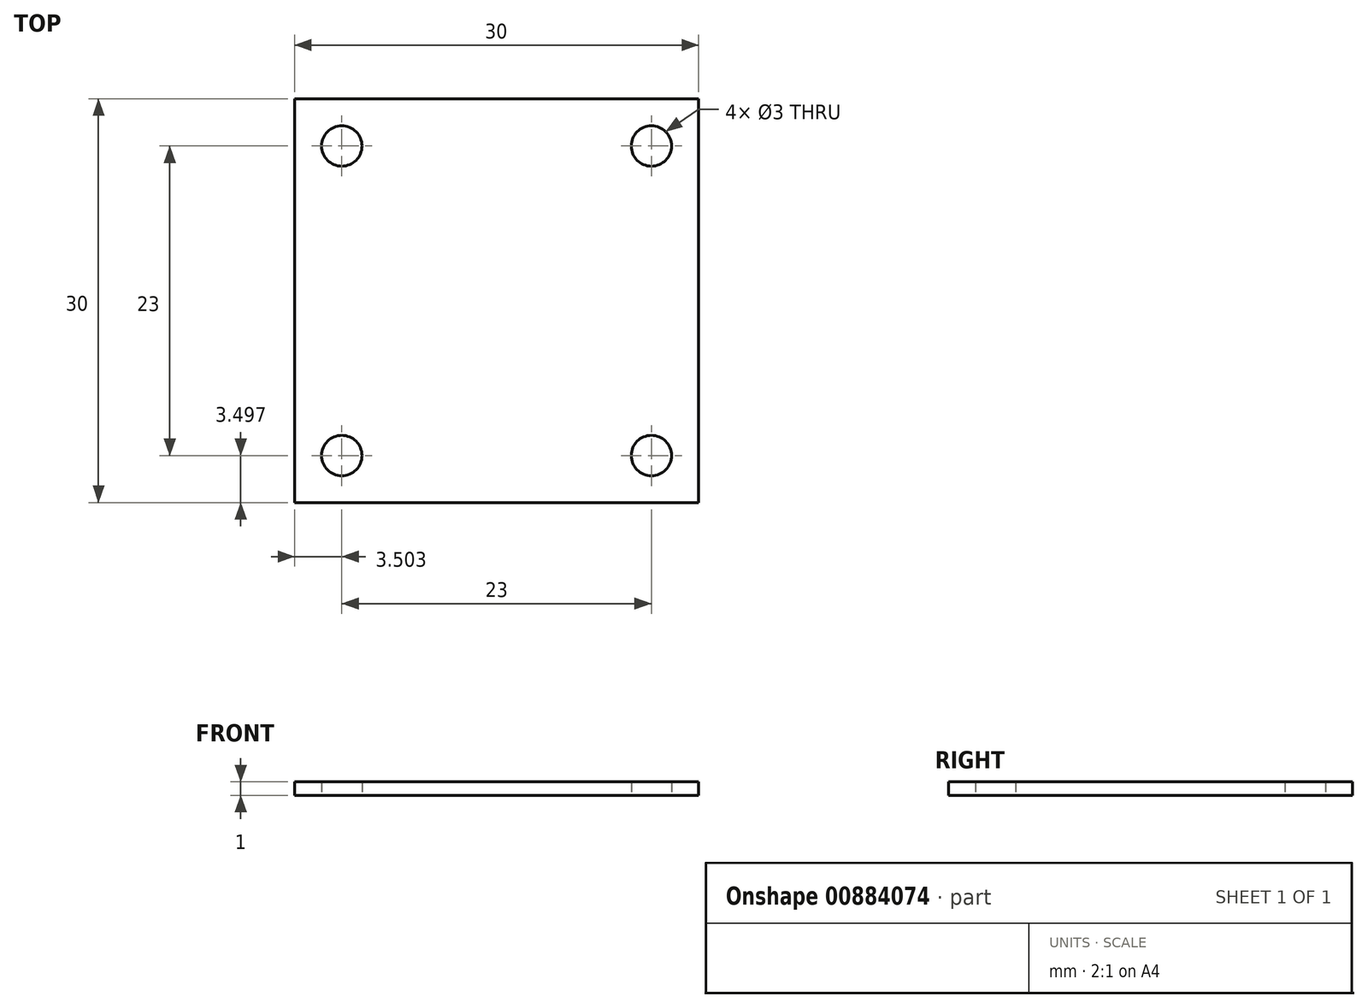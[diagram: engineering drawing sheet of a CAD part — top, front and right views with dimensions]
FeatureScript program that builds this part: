
annotation { "Feature Type Name" : "Feature", "Feature Type Description" : "" }
export const myFeature = defineFeature(function(context is Context, id is Id, definition is map)
    precondition{}
    {
        {
            var Q0;
            Q0=qCreatedBy(makeId("Top.planeOp"),FACE);
            var sketch = newSketch(context, id + "F0", { "sketchPlane" : qUnion([Q0])});
            skLineSegment(sketch, "E0.bottom", {"start": v(-40.86, 10.92) * mm, "end": v(-10.86, 10.92) * mm});
            skLineSegment(sketch, "E0.top", {"start": v(-40.86, -19.08) * mm, "end": v(-10.86, -19.08) * mm});
            skLineSegment(sketch, "E0.left", {"start": v(-40.86, 10.92) * mm, "end": v(-40.86, -19.08) * mm});
            skLineSegment(sketch, "E0.right", {"start": v(-10.86, 10.92) * mm, "end": v(-10.86, -19.08) * mm});
            skCircle(sketch, "E1", {"center": v(-14.36, 7.42) * mm, "radius": 1.5 * mm});
            skCircle(sketch, "E2.MirrorC", {"center": v(-37.36, 7.42) * mm, "radius": 1.5 * mm});
            skCircle(sketch, "E3.MirrorC", {"center": v(-14.36, -15.58) * mm, "radius": 1.5 * mm});
            skCircle(sketch, "E4.MirrorC", {"center": v(-37.36, -15.58) * mm, "radius": 1.5 * mm});
            skSolve(sketch);
        }
        {
            var Q0;
            Q0 = qSketchRegion(id + "F0", true);
            extrude(context, id + "F1", {"entities" : qUnion([Q0]), "depth" : 1 * mm, "offsetDistance" : 25 * mm});
        }
    });
